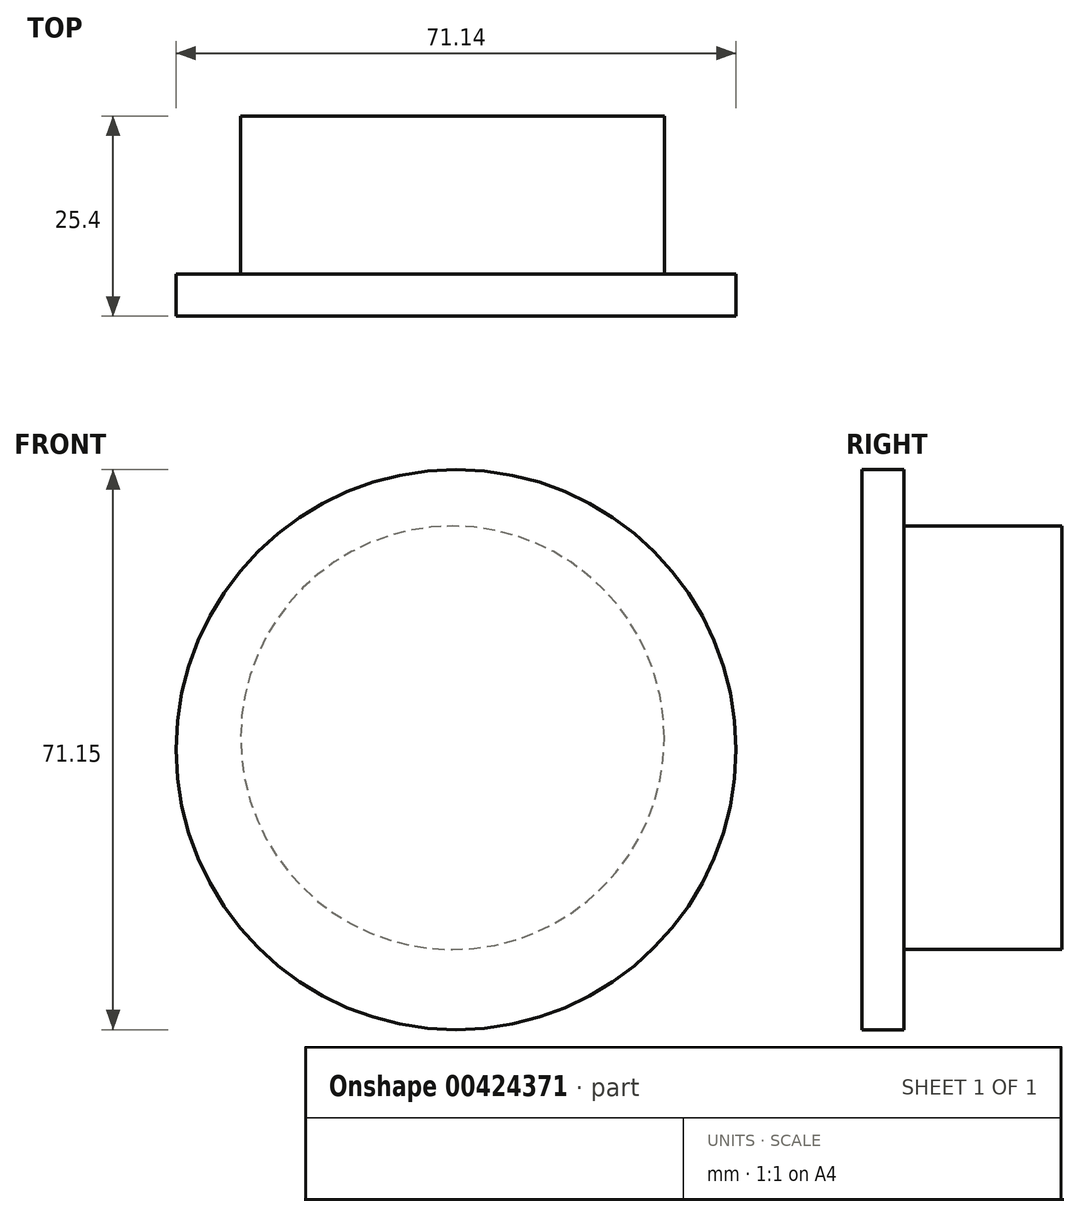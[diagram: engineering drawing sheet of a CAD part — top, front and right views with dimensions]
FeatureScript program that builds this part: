
annotation { "Feature Type Name" : "Feature", "Feature Type Description" : "" }
export const myFeature = defineFeature(function(context is Context, id is Id, definition is map)
    precondition{}
    {
        {
            var Q0;
            Q0=qCreatedBy(makeId("Front.planeOp"),FACE);
            var sketch = newSketch(context, id + "F0", { "sketchPlane" : qUnion([Q0])});
            skCircle(sketch, "E0", {"center": v(32.58, 14.28) * mm, "radius": 35.57 * mm});
            skPoint(sketch, "E0.first.point", {"position": v(0, 0) * mm});
            skPoint(sketch, "E0.second.point", {"position": v(68.04, 17.15) * mm});
            skPoint(sketch, "E0.third.point", {"position": v(5.44, 37.28) * mm});
            skSolve(sketch);
        }
        {
            var Q0;
            Q0 = qSketchRegion(id + "F0", true);
            extrude(context, id + "F1", {"entities" : qUnion([Q0]), "depth" : 5.33 * mm});
        }
        {
            var Q0;
            Q0=qCreatedBy(makeId("Front.planeOp"),FACE);
            var sketch = newSketch(context, id + "F2", { "sketchPlane" : qUnion([Q0])});
            skCircle(sketch, "E1", {"center": v(32.11, 15.78) * mm, "radius": 26.9 * mm});
            skSolve(sketch);
        }
        {
            var Q0;
            Q0 = qSketchRegion(id + "F2", true);
            extrude(context, id + "F3", {"entities" : qUnion([Q0]), "operationType" : NewBodyOperationType.ADD, "oppositeDirection" : true, "depth" : 20.07 * mm});
        }
    });
